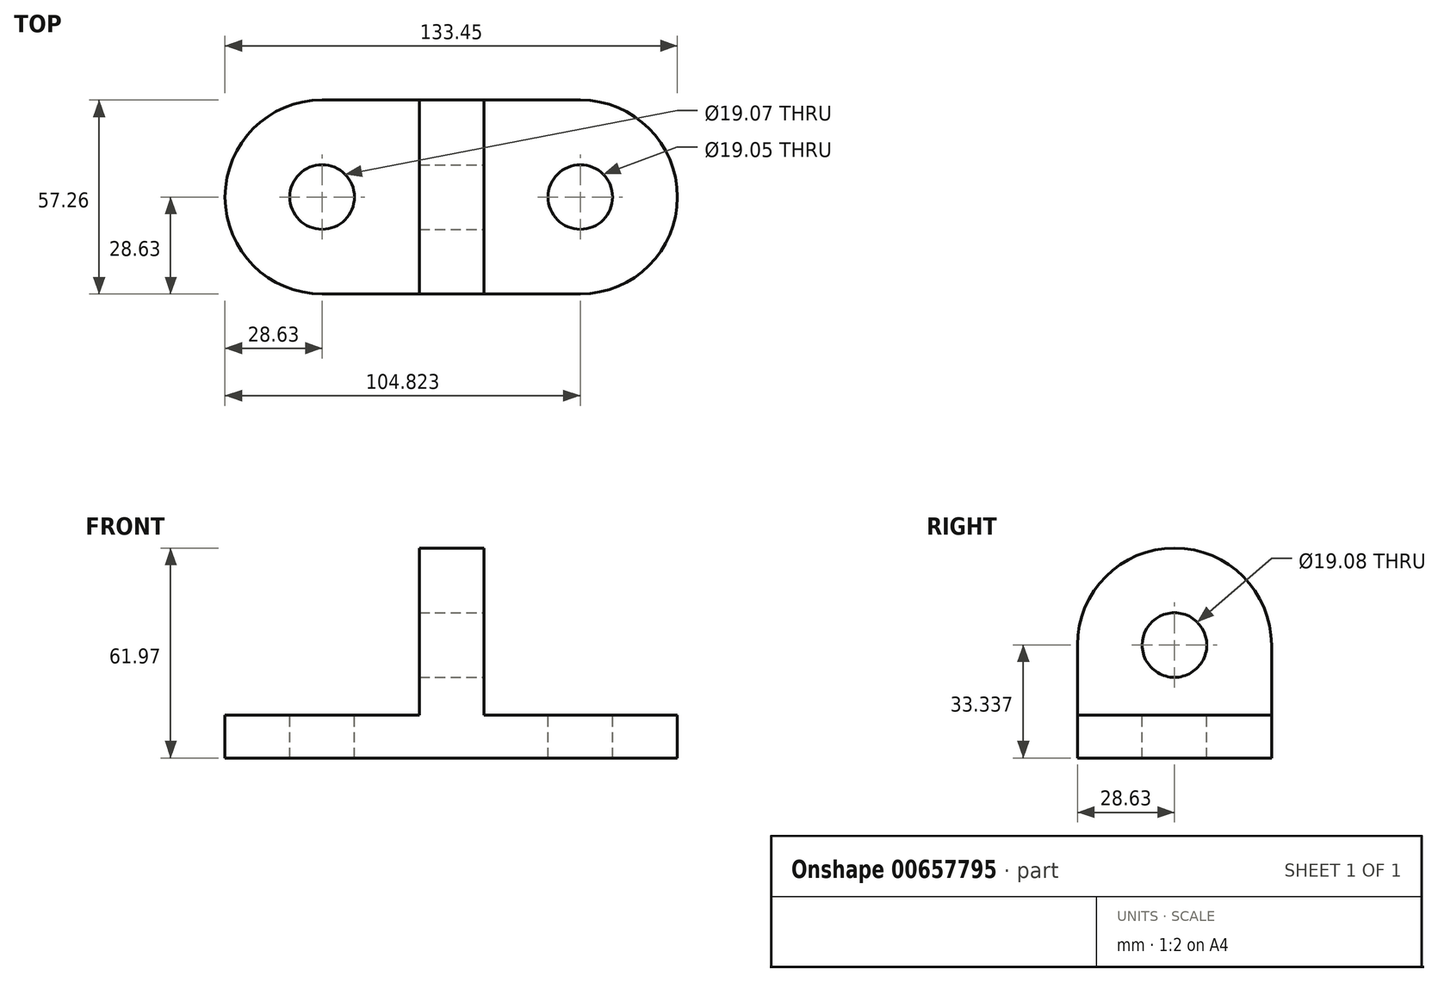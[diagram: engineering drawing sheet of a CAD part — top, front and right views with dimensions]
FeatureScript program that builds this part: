
annotation { "Feature Type Name" : "Feature", "Feature Type Description" : "" }
export const myFeature = defineFeature(function(context is Context, id is Id, definition is map)
    precondition{}
    {
        {
            var Q0;
            Q0=qCreatedBy(makeId("Top.planeOp"),FACE);
            var sketch = newSketch(context, id + "F0", { "sketchPlane" : qUnion([Q0])});
            skLineSegment(sketch, "E0", {"start": v(0, 0) * mm, "end": v(76.2, 0) * mm});
            skLineSegment(sketch, "E1", {"start": v(76.2, 0) * mm, "end": v(76.2, 57.26) * mm});
            skLineSegment(sketch, "E2", {"start": v(76.2, 57.26) * mm, "end": v(0, 57.26) * mm});
            skLineSegment(sketch, "E3", {"start": v(0, 57.26) * mm, "end": v(0, 0) * mm});
            skArc(sketch, "E4", {"start": v(0, 57.26) * mm, "mid": v(-28.63, 28.63) * mm, "end": v(0, 0) * mm});
            skArc(sketch, "E5", {"start": v(76.2, 0) * mm, "mid": v(104.82, 28.63) * mm, "end": v(76.2, 57.26) * mm});
            skSolve(sketch);
        }
        {
            var Q0;
            Q0=makeQuery(id+"F0.imprint","IMPRINT",FACE,{"disambiguationData":[TD([[makeQuery(id+"F0.imprint","IMPRINT",EDGE,{"derivedFrom":sQuery(id+"F0.wireOp",EDGE,"E1")}),-1.0]])]});
            var Q1;
            Q1=makeQuery(id+"F0.imprint","IMPRINT",FACE,{"disambiguationData":[TD([[makeQuery(id+"F0.imprint","IMPRINT",EDGE,{"derivedFrom":sQuery(id+"F0.wireOp",EDGE,"E3")}),-1.0]])]});
            var Q2;
            Q2=makeQuery(id+"F0.imprint","IMPRINT",FACE,{"disambiguationData":[TD([[makeQuery(id+"F0.imprint","IMPRINT",EDGE,{"derivedFrom":sQuery(id+"F0.wireOp",EDGE,"E0")}),1.0]])]});
            extrude(context, id + "F1", {"entities" : qUnion([Q0, Q1, Q2]), "oppositeDirection" : true, "depth" : 12.7 * mm, "offsetDistance" : 25.4 * mm});
        }
        {
            var Q0;
            Q0=makeQuery(id+"F1.opExtrude","CAP_FACE",FACE,{"disambiguationData":[OSD([sQuery(id+"F0.wireOp",EDGE,"E0"),sQuery(id+"F0.wireOp",EDGE,"E2"),sQuery(id+"F0.wireOp",EDGE,"E4"),sQuery(id+"F0.wireOp",EDGE,"E5")])],"isStart":true});
            var sketch = newSketch(context, id + "F2", { "sketchPlane" : qUnion([Q0])});
            skLineSegment(sketch, "E6", {"start": v(76.2, 0) * mm, "end": v(47.78, 0) * mm});
            skLineSegment(sketch, "E7", {"start": v(47.78, 0) * mm, "end": v(47.78, 57.26) * mm});
            skLineSegment(sketch, "E8", {"start": v(47.78, 57.26) * mm, "end": v(28.75, 57.26) * mm});
            skLineSegment(sketch, "E9", {"start": v(28.75, 57.26) * mm, "end": v(28.75, 0) * mm});
            skLineSegment(sketch, "E10", {"start": v(28.75, 0) * mm, "end": v(47.78, 0) * mm});
            skSolve(sketch);
        }
        {
            var Q0;
            Q0=makeQuery(id+"F2.imprint","IMPRINT",FACE,{"disambiguationData":[TD([[makeQuery(id+"F2.imprint","IMPRINT",EDGE,{"derivedFrom":sQuery(id+"F2.wireOp",EDGE,"E7")}),1.0]])]});
            extrude(context, id + "F3", {"entities" : qUnion([Q0]), "operationType" : NewBodyOperationType.ADD, "depth" : 20.64 * mm, "offsetDistance" : 25.4 * mm});
        }
        {
            var Q0;
            Q0=makeQuery(id+"F3.opExtrude","SWEPT_FACE",FACE,{"disambiguationData":[OSD([sQuery(id+"F2.wireOp",EDGE,"E9")])]});
            var sketch = newSketch(context, id + "F4", { "sketchPlane" : qUnion([Q0])});
            skArc(sketch, "E11", {"start": v(0, 20.64) * mm, "mid": v(-28.63, 49.27) * mm, "end": v(-57.26, 20.64) * mm});
            skSolve(sketch);
        }
        {
            var Q0;
            Q0 = qSketchRegion(id + "F4", true);
            var Q1;
            Q1=makeQuery(id+"F4.imprint","IMPRINT",FACE,{"disambiguationData":[TD([[makeQuery(id+"F4.imprint","IMPRINT",EDGE,{"derivedFrom":sQuery(id+"F4.wireOp",EDGE,"E11")}),1.0]])]});
            extrude(context, id + "F5", {"entities" : qUnion([Q0, Q1]), "operationType" : NewBodyOperationType.ADD, "oppositeDirection" : true, "depth" : 19.02 * mm, "offsetDistance" : 25.4 * mm});
        }
        {
            var Q0;
            Q0=makeQuery(id+"F3.opExtrude","SWEPT_FACE",FACE,{"disambiguationData":[OSD([sQuery(id+"F2.wireOp",EDGE,"E7")])]});
            var sketch = newSketch(context, id + "F6", { "sketchPlane" : qUnion([Q0])});
            skLineSegment(sketch, "E12", {"start": v(0, 20.64) * mm, "end": v(57.26, 20.64) * mm});
            skLineSegment(sketch, "E13", {"start": v(28.63, 0) * mm, "end": v(28.63, 20.64) * mm});
            skCircle(sketch, "E14", {"center": v(28.63, 20.64) * mm, "radius": 9.54 * mm});
            skSolve(sketch);
        }
        {
            var Q0;
            {var subQ0=sQuery(id+"F6.wireOp",EDGE,"E13");var subQ1=sQuery(id+"F6.wireOp",EDGE,"E12");var subQ2=makeQuery(id+"F6.imprint","INTERSECT",VERTEX,{"derivedFrom":[subQ1,subQ0]});Q0=makeQuery(id+"F6.imprint","IMPRINT",FACE,{"disambiguationData":[TD([[makeQuery(id+"F6.imprint","IMPRINT",EDGE,{"disambiguationData":[TD([[subQ2,-1.0]])],"derivedFrom":subQ1}),1.0]])]});}
            var Q1;
            {var subQ0=sQuery(id+"F6.wireOp",EDGE,"E12");var subQ1=makeQuery(id+"F6.imprint","INTERSECT",VERTEX,{"derivedFrom":[subQ0,sQuery(id+"F6.wireOp",EDGE,"E13")]});Q1=makeQuery(id+"F6.imprint","IMPRINT",FACE,{"disambiguationData":[TD([[makeQuery(id+"F6.imprint","IMPRINT",EDGE,{"disambiguationData":[TD([[subQ1,1.0]])],"derivedFrom":subQ0}),-1.0]])]});}
            var Q2;
            {var subQ0=sQuery(id+"F6.wireOp",EDGE,"E13");var subQ1=sQuery(id+"F6.wireOp",EDGE,"E12");var subQ2=makeQuery(id+"F6.imprint","INTERSECT",VERTEX,{"derivedFrom":[subQ1,subQ0]});Q2=makeQuery(id+"F6.imprint","IMPRINT",FACE,{"disambiguationData":[TD([[makeQuery(id+"F6.imprint","IMPRINT",EDGE,{"disambiguationData":[TD([[subQ2,1.0]])],"derivedFrom":subQ1}),1.0]])]});}
            extrude(context, id + "F7", {"entities" : qUnion([Q0, Q1, Q2]), "operationType" : NewBodyOperationType.REMOVE, "oppositeDirection" : true, "depth" : 19.05 * mm, "offsetDistance" : 25.4 * mm});
        }
        {
            var Q0;
            {var subQ0=sQuery(id+"F0.wireOp",EDGE,"E4");var subQ1=sQuery(id+"F0.wireOp",EDGE,"E2");var subQ2=sQuery(id+"F0.wireOp",EDGE,"E0");Q0=makeQuery(id+"F3.boolean.opBoolean","SPLIT",FACE,{"disambiguationData":[TD([makeQuery(id+"F1.opExtrude","SWEPT_FACE",FACE,{"disambiguationData":[OSD([subQ0])]})])],"derivedFrom":makeQuery(id+"F1.opExtrude","CAP_FACE",FACE,{"disambiguationData":[OSD([subQ2,subQ1,subQ0,sQuery(id+"F0.wireOp",EDGE,"E5")])],"isStart":true})});}
            var sketch = newSketch(context, id + "F8", { "sketchPlane" : qUnion([Q0])});
            skCircle(sketch, "E15", {"center": v(0, 28.63) * mm, "radius": 9.54 * mm});
            skSolve(sketch);
        }
        {
            var Q0;
            Q0=makeQuery(id+"F8.imprint","IMPRINT",FACE,{"disambiguationData":[TD([[makeQuery(id+"F8.imprint","IMPRINT",EDGE,{"derivedFrom":sQuery(id+"F8.wireOp",EDGE,"E15")}),1.0]])]});
            extrude(context, id + "F9", {"entities" : qUnion([Q0]), "operationType" : NewBodyOperationType.REMOVE, "oppositeDirection" : true, "depth" : 12.7 * mm, "offsetDistance" : 25.4 * mm});
        }
        {
            var Q0;
            {var subQ0=sQuery(id+"F0.wireOp",EDGE,"E2");var subQ1=sQuery(id+"F0.wireOp",EDGE,"E5");var subQ2=sQuery(id+"F0.wireOp",EDGE,"E0");Q0=makeQuery(id+"F3.boolean.opBoolean","SPLIT",FACE,{"disambiguationData":[TD([makeQuery(id+"F1.opExtrude","SWEPT_FACE",FACE,{"disambiguationData":[OSD([subQ1])]})])],"derivedFrom":makeQuery(id+"F1.opExtrude","CAP_FACE",FACE,{"disambiguationData":[OSD([subQ2,subQ0,sQuery(id+"F0.wireOp",EDGE,"E4"),subQ1])],"isStart":true})});}
            var sketch = newSketch(context, id + "F10", { "sketchPlane" : qUnion([Q0])});
            skLineSegment(sketch, "E16", {"start": v(76.2, 57.26) * mm, "end": v(76.2, 28.63) * mm});
            skLineSegment(sketch, "E17", {"start": v(76.2, 28.63) * mm, "end": v(104.82, 28.63) * mm});
            skCircle(sketch, "E18", {"center": v(76.2, 28.63) * mm, "radius": 9.53 * mm});
            skSolve(sketch);
        }
        {
            var Q0;
            {var subQ0=sQuery(id+"F10.wireOp",EDGE,"E17");var subQ1=sQuery(id+"F10.wireOp",EDGE,"E16");var subQ2=makeQuery(id+"F10.imprint","INTERSECT",VERTEX,{"derivedFrom":[subQ1,subQ0]});Q0=makeQuery(id+"F10.imprint","IMPRINT",FACE,{"disambiguationData":[TD([[makeQuery(id+"F10.imprint","IMPRINT",EDGE,{"disambiguationData":[TD([[subQ2,1.0]])],"derivedFrom":subQ1}),-1.0]])]});}
            var Q1;
            {var subQ0=sQuery(id+"F10.wireOp",EDGE,"E17");var subQ1=sQuery(id+"F10.wireOp",EDGE,"E16");var subQ2=makeQuery(id+"F10.imprint","INTERSECT",VERTEX,{"derivedFrom":[subQ1,subQ0]});Q1=makeQuery(id+"F10.imprint","IMPRINT",FACE,{"disambiguationData":[TD([[makeQuery(id+"F10.imprint","IMPRINT",EDGE,{"disambiguationData":[TD([[subQ2,1.0]])],"derivedFrom":subQ1}),1.0]])]});}
            extrude(context, id + "F11", {"entities" : qUnion([Q0, Q1]), "operationType" : NewBodyOperationType.REMOVE, "oppositeDirection" : true, "depth" : 25.4 * mm, "offsetDistance" : 25.4 * mm});
        }
        {
            var Q0;
            {var subQ0=sQuery(id+"F10.wireOp",EDGE,"E17");var subQ1=sQuery(id+"F10.wireOp",EDGE,"E16");var subQ2=makeQuery(id+"F10.imprint","INTERSECT",VERTEX,{"derivedFrom":[subQ1,subQ0]});Q0=makeQuery(id+"F10.imprint","IMPRINT",FACE,{"disambiguationData":[TD([[makeQuery(id+"F10.imprint","IMPRINT",EDGE,{"disambiguationData":[TD([[subQ2,1.0]])],"derivedFrom":subQ1}),1.0]])]});}
            var Q1;
            {var subQ0=sQuery(id+"F10.wireOp",EDGE,"E17");var subQ1=sQuery(id+"F10.wireOp",EDGE,"E16");var subQ2=makeQuery(id+"F10.imprint","INTERSECT",VERTEX,{"derivedFrom":[subQ1,subQ0]});Q1=makeQuery(id+"F10.imprint","IMPRINT",FACE,{"disambiguationData":[TD([[makeQuery(id+"F10.imprint","IMPRINT",EDGE,{"disambiguationData":[TD([[subQ2,1.0]])],"derivedFrom":subQ1}),-1.0]])]});}
            extrude(context, id + "F12", {"entities" : qUnion([Q0, Q1]), "operationType" : NewBodyOperationType.REMOVE, "oppositeDirection" : true, "depth" : 25.4 * mm, "offsetDistance" : 25.4 * mm});
        }
    });
